# Revit family: leddownlightrc-hz_r200-16w-dim-4000-wh_140051481
name_source: partatom
category: Leuchten
revit_build: Autodesk Revit 2016 (Build: 20190508_0715(x64)
units: mm (PartAtom-declared; Revit-internal decimal feet)

## family parameters
Basisbauteil = Fläche
Beim Laden mit Abzugskörper schneiden = Nein
Bemaßung runder Anschluss = Durchmesser verwenden
Gemeinsam genutzt = Nein
Lichtquelle = Nein
Raumberechnungspunkt = Nein
Teiletyp = Normal

## types (1)
- LEDDownlightRc-HZ R200-16W-Dim-4000-WH (1 x LED, 1500 lm)
    Approval mark = CE
    Beschreibung = Compact dimmable LED downlight. Easy switching from CFL to LED – even when dimming is needed. Integrated driver for easier installation. IP44 on light emitting side.
    CIE Flux Codes = 47 79 96 100 100
    Control Gear = Electronic ballast
    Height = 0 mm  [stored 0 ft]
    Hersteller = OPPLE
    Lamp Light Flux = 1500 lm
    Lamp count = 1
    Lampe = 1 x LED
    Length = 213 mm
    Luminous efficacy = 94 lm/W
    ModVariant = Nein
    Modell = 140051481
    Mounting Place = Ceiling
    Mounting Type = Recessed
    Number of Poles = 1
    OnlyDefault = Ja
    Power Factor = 1
    Product Name = LEDDownlightRc-HZ R200-16W-Dim-4000-WH
    Product group = Downlight HZ<sup>DIM</sup>
    ProductGroupID = 402
    Protection Class = Protection class II
    Protection Degree = IP 44
    RLX_Detail_Level = 1
    RlxData = <blob elided: 28465 chars, md5=662449fe>
    Scheinlast = 16 VA
    Socket = socket
    Standby Power = 0 W
    System Light Flux = 1500 lm
    System Power = 16 W
    Typenbild = 140051481.jpg
    Typenkommentare = Product without accessories
    URL = http://relux.com
    VarID = ---
    Voltage = 0 V
    Vorgabe-Ansicht = 1800 mm
    Weight = 0.00 kg
    Width = 0 mm  [stored 0 ft]

note: [stored X ft] marks values corroborated as IEEE doubles in the binary element streams (Revit-internal decimal feet)

## geometry (parser evidence)
native form markers: Blend x4, Sweep x14
no freeform markers — native parametric forms only
